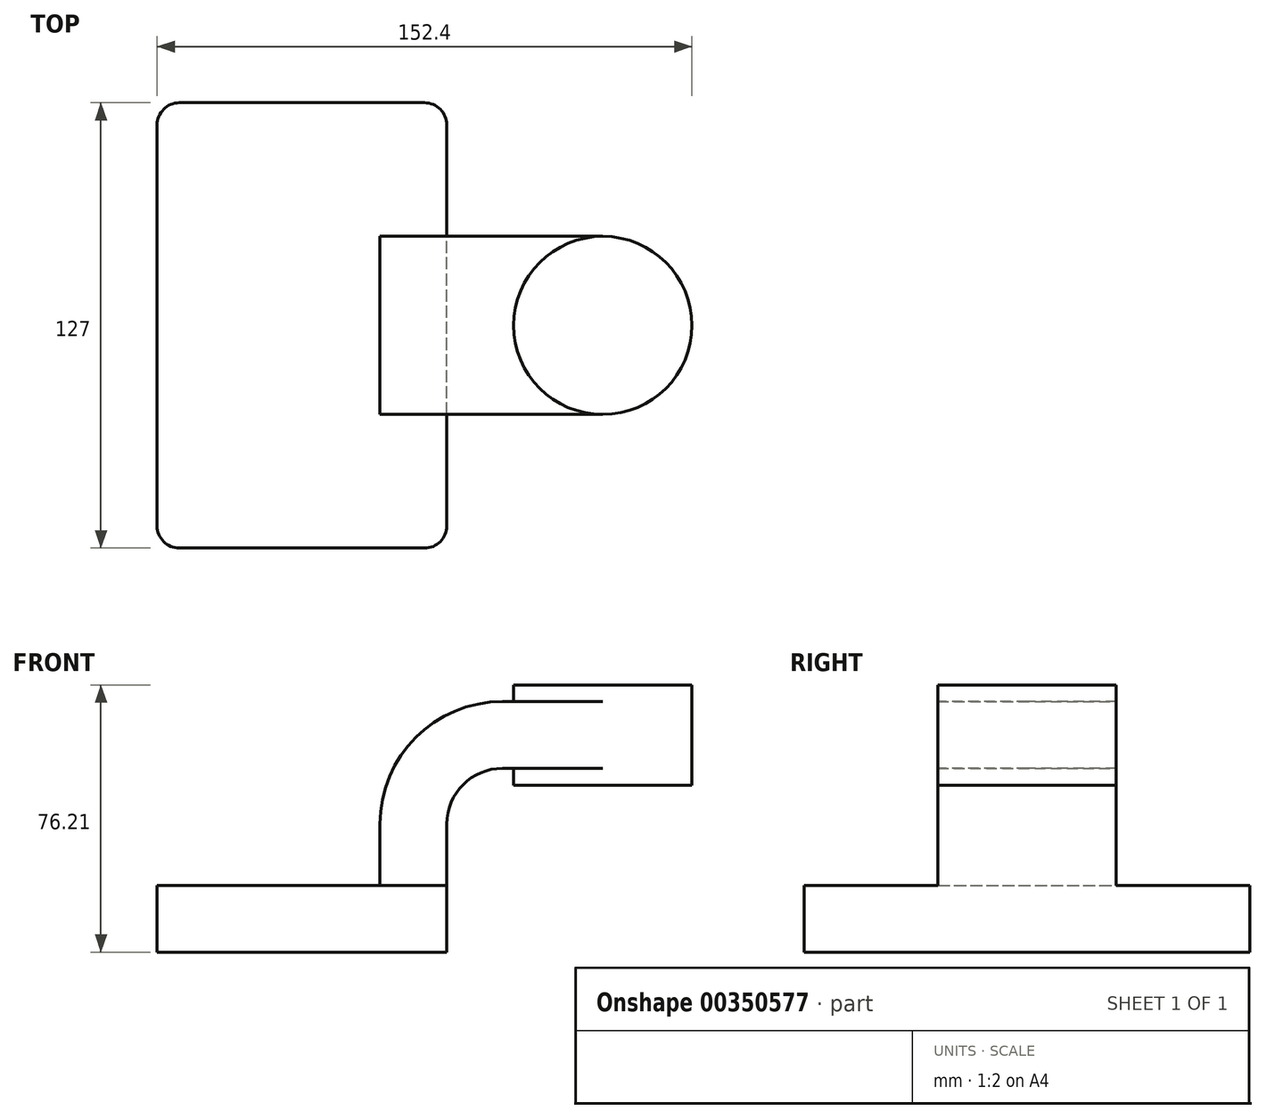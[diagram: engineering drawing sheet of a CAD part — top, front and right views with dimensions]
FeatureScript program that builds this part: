
annotation { "Feature Type Name" : "Feature", "Feature Type Description" : "" }
export const myFeature = defineFeature(function(context is Context, id is Id, definition is map)
    precondition{}
    {
        {
            var Q0;
            Q0=qCreatedBy(makeId("Front.planeOp"),FACE);
            var sketch = newSketch(context, id + "F0", { "sketchPlane" : qUnion([Q0])});
            skLineSegment(sketch, "E0.bottom", {"start": v(-41.28, -9.52) * mm, "end": v(41.28, -9.52) * mm});
            skLineSegment(sketch, "E0.top", {"start": v(-41.28, 9.53) * mm, "end": v(41.28, 9.53) * mm});
            skLineSegment(sketch, "E0.left", {"start": v(-41.28, -9.52) * mm, "end": v(-41.28, 9.53) * mm});
            skLineSegment(sketch, "E0.right", {"start": v(41.28, -9.53) * mm, "end": v(41.28, 9.52) * mm});
            skPoint(sketch, "E0.middle", {"position": v(0, 0) * mm});
            skLineSegment(sketch, "E1.bottom", {"start": v(60.33, 38.1) * mm, "end": v(111.13, 38.1) * mm});
            skLineSegment(sketch, "E1.top", {"start": v(60.33, 66.68) * mm, "end": v(111.12, 66.68) * mm});
            skLineSegment(sketch, "E1.left", {"start": v(60.33, 38.1) * mm, "end": v(60.33, 66.68) * mm});
            skLineSegment(sketch, "E1.right", {"start": v(111.13, 38.1) * mm, "end": v(111.12, 66.68) * mm});
            skPoint(sketch, "E1.middle", {"position": v(85.73, 52.39) * mm});
            skLineSegment(sketch, "E2", {"start": v(41.28, 9.52) * mm, "end": v(41.28, 27) * mm});
            skArc(sketch, "E3", {"start": v(41.28, 27) * mm, "mid": v(45.92, 38.23) * mm, "end": v(57.15, 42.88) * mm});
            skLineSegment(sketch, "E4", {"start": v(57.15, 42.88) * mm, "end": v(85.72, 42.88) * mm});
            skLineSegment(sketch, "E5.0", {"start": v(57.15, 61.93) * mm, "end": v(85.72, 61.93) * mm});
            skArc(sketch, "E5.1", {"start": v(22.23, 27) * mm, "mid": v(32.45, 51.7) * mm, "end": v(57.15, 61.93) * mm});
            skLineSegment(sketch, "E5.2", {"start": v(22.23, 9.52) * mm, "end": v(22.23, 27) * mm});
            skLineSegment(sketch, "E6", {"start": v(85.72, 38.1) * mm, "end": v(85.72, 66.68) * mm});
            skFitSpline(sketch, "E7", {"points": [v(-41.28, 9.53) * mm, v(57.15, 61.93) * mm], "startDerivative": vector(-1.14, 103.04) * mm, "endDerivative": vector(102.52, -6.71) * mm});
            skSolve(sketch);
        }
        {
            var Q0;
            Q0=makeQuery(id+"F0.imprint","IMPRINT",FACE,{"disambiguationData":[TD([[makeQuery(id+"F0.imprint","IMPRINT",EDGE,{"derivedFrom":sQuery(id+"F0.wireOp",EDGE,"E0.bottom")}),1.0]])]});
            extrude(context, id + "F1", {"entities" : qUnion([Q0]), "depth" : 127 * mm, "symmetric" : true});
        }
        {
            var Q0;
            {var subQ1=sQuery(id+"F0.wireOp",EDGE,"E2");Q0=makeQuery(id+"F0.imprint","IMPRINT",FACE,{"disambiguationData":[TD([[makeQuery(id+"F0.imprint","IMPRINT",EDGE,{"derivedFrom":subQ1}),1.0]])]});}
            var Q1;
            {var subQ0=sQuery(id+"F0.wireOp",EDGE,"E4");var subQ1=sQuery(id+"F0.wireOp",EDGE,"E1.left");var subQ2=makeQuery(id+"F0.imprint","INTERSECT",VERTEX,{"derivedFrom":[subQ1,subQ0]});Q1=makeQuery(id+"F0.imprint","IMPRINT",FACE,{"disambiguationData":[TD([[makeQuery(id+"F0.imprint","IMPRINT",EDGE,{"disambiguationData":[TD([[subQ2,-1.0]])],"derivedFrom":subQ1}),-1.0]])]});}
            extrude(context, id + "F2", {"entities" : qUnion([Q0, Q1]), "operationType" : NewBodyOperationType.ADD, "depth" : 50.8 * mm, "symmetric" : true});
        }
        {
            var Q0;
            Q0=makeQuery(id+"F0.imprint","IMPRINT",FACE,{"disambiguationData":[TD([[makeQuery(id+"F0.imprint","IMPRINT",EDGE,{"derivedFrom":sQuery(id+"F0.wireOp",EDGE,"E5.1")}),1.0]])]});
            extrude(context, id + "F3", {"entities" : qUnion([Q0]), "operationType" : NewBodyOperationType.ADD, "oppositeDirection" : true, "depth" : 15.88 * mm, "symmetric" : true});
        }
        {
            var Q0;
            {var subQ0=sQuery(id+"F0.wireOp",EDGE,"E1.right");Q0=makeQuery(id+"F0.imprint","IMPRINT",FACE,{"disambiguationData":[TD([[makeQuery(id+"F0.imprint","IMPRINT",EDGE,{"derivedFrom":subQ0}),1.0]])]});}
            var Q1;
            Q1=sQuery(id+"F0.wireOp",EDGE,"E6");
            revolve(context, id + "F4", {"operationType" : NewBodyOperationType.ADD, "entities" : qUnion([Q0]), "axis" : qUnion([Q1]), "revolveType" : RevolveType.FULL});
        }
        {
            var Q0;
            Q0=makeQuery(id+"F1.opExtrude","CAP_EDGE",EDGE,{"disambiguationData":[OSD([sQuery(id+"F0.wireOp",EDGE,"E0.right")])],"isStart":false});
            var Q1;
            Q1=makeQuery(id+"F1.opExtrude","CAP_EDGE",EDGE,{"disambiguationData":[OSD([sQuery(id+"F0.wireOp",EDGE,"E0.left")])],"isStart":false});
            var Q2;
            Q2=makeQuery(id+"F1.opExtrude","CAP_EDGE",EDGE,{"disambiguationData":[OSD([sQuery(id+"F0.wireOp",EDGE,"E0.right")])],"isStart":true});
            var Q3;
            Q3=makeQuery(id+"F1.opExtrude","CAP_EDGE",EDGE,{"disambiguationData":[OSD([sQuery(id+"F0.wireOp",EDGE,"E0.left")])],"isStart":true});
            fillet(context, id + "F5", {"entities" : qUnion([Q0, Q1, Q2, Q3]), "radius" : 6.35 * mm, "tangentPropagation" : true, "allowEdgeOverflow" : false});
        }
    });
